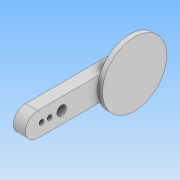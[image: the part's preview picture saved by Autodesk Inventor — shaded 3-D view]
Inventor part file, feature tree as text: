
AUTODESK INVENTOR PART (.ipt)
format: ipt  version: 2021 (Build 250183000, 183)  size: 120,832 bytes
history: native  units: mm
features: extrude x2, fillet x2, sketch x2, other x1, projected_geometry x1
ambient origin geometry x8: Origin, YZ Plane, XZ Plane, XY Plane, X Axis, Y Axis, Z Axis, Center Point
bodies: Body1 (feature_tree)
feature tree (8):
  other  "實體1"
  extrude  "擠出1"  Depth=150.0mm
  fillet  "圓角1"  Radius=300.0mm
  extrude  "擠出2"  Depth=200.0mm
  fillet  "圓角2"  Radius=50.0mm
  sketch  "草圖1"
  sketch  "草圖2"
  projected_geometry  "投影迴路1"
